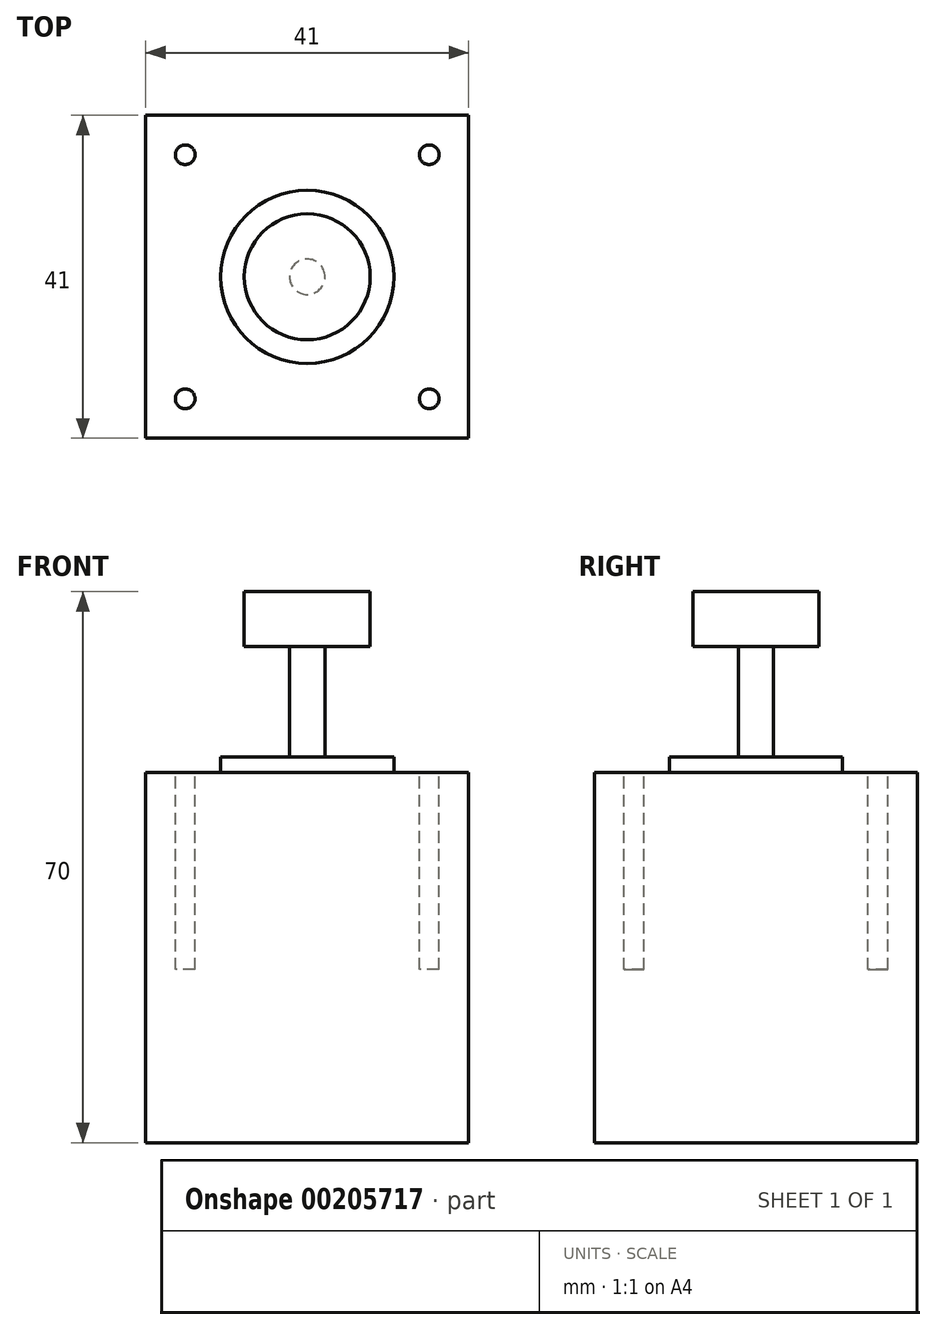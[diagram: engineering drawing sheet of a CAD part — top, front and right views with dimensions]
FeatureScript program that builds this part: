
annotation { "Feature Type Name" : "Feature", "Feature Type Description" : "" }
export const myFeature = defineFeature(function(context is Context, id is Id, definition is map)
    precondition{}
    {
        {
            var Q0;
            Q0=qCreatedBy(makeId("Top.planeOp"),FACE);
            var sketch = newSketch(context, id + "F0", { "sketchPlane" : qUnion([Q0])});
            skLineSegment(sketch, "E0.bottom", {"start": v(0, 0) * mm, "end": v(41, 0) * mm});
            skLineSegment(sketch, "E0.top", {"start": v(0, 41) * mm, "end": v(41, 41) * mm});
            skLineSegment(sketch, "E0.left", {"start": v(0, 0) * mm, "end": v(0, 41) * mm});
            skLineSegment(sketch, "E0.right", {"start": v(41, 0) * mm, "end": v(41, 41) * mm});
            skSolve(sketch);
        }
        {
            var Q0;
            Q0 = qSketchRegion(id + "F0", true);
            extrude(context, id + "F1", {"entities" : qUnion([Q0]), "depth" : 47 * mm});
        }
        {
            var Q0;
            Q0=makeQuery(id+"F1.opExtrude","CAP_FACE",FACE,{"disambiguationData":[OSD([sQuery(id+"F0.wireOp",EDGE,"E0.bottom"),sQuery(id+"F0.wireOp",EDGE,"E0.top"),sQuery(id+"F0.wireOp",EDGE,"E0.left"),sQuery(id+"F0.wireOp",EDGE,"E0.right")])],"isStart":false});
            var sketch = newSketch(context, id + "F2", { "sketchPlane" : qUnion([Q0])});
            skCircle(sketch, "E1", {"center": v(5, 5) * mm, "radius": 1.25 * mm});
            skLineSegment(sketch, "E2", {"start": v(0, 20.5) * mm, "end": v(20.5, 20.5) * mm, "construction": true});
            skPoint(sketch, "E2.endSnap0", {"position": v(20.5, 0) * mm});
            skLineSegment(sketch, "E3", {"start": v(20.5, 20.5) * mm, "end": v(20.5, 0) * mm, "construction": true});
            skCircle(sketch, "E4.1.0", {"center": v(36, 5) * mm, "radius": 1.25 * mm});
            skCircle(sketch, "E4.2.0", {"center": v(36, 36) * mm, "radius": 1.25 * mm});
            skCircle(sketch, "E4.3.0", {"center": v(5, 36) * mm, "radius": 1.25 * mm});
            skPoint(sketch, "E4.center", {"position": v(20.5, 20.5) * mm});
            skLineSegment(sketch, "E5", {"start": v(36, 36) * mm, "end": v(36, 5) * mm, "construction": true});
            skSolve(sketch);
        }
        {
            var Q0;
            Q0 = qSketchRegion(id + "F2", true);
            extrude(context, id + "F3", {"entities" : qUnion([Q0]), "operationType" : NewBodyOperationType.REMOVE, "oppositeDirection" : true, "depth" : 25 * mm});
        }
        {
            var Q0;
            Q0=makeQuery(id+"F1.opExtrude","CAP_FACE",FACE,{"disambiguationData":[OSD([sQuery(id+"F0.wireOp",EDGE,"E0.bottom"),sQuery(id+"F0.wireOp",EDGE,"E0.top"),sQuery(id+"F0.wireOp",EDGE,"E0.left"),sQuery(id+"F0.wireOp",EDGE,"E0.right")])],"isStart":false});
            var sketch = newSketch(context, id + "F4", { "sketchPlane" : qUnion([Q0])});
            skLineSegment(sketch, "E6", {"start": v(0, 20.5) * mm, "end": v(20.5, 20.5) * mm, "construction": true});
            skPoint(sketch, "E6.endSnap0", {"position": v(20.5, 0) * mm});
            skCircle(sketch, "E7", {"center": v(20.5, 20.5) * mm, "radius": 11 * mm});
            skSolve(sketch);
        }
        {
            var Q0;
            Q0 = qSketchRegion(id + "F4", true);
            extrude(context, id + "F5", {"entities" : qUnion([Q0]), "operationType" : NewBodyOperationType.ADD, "depth" : 2 * mm});
        }
        {
            var Q0;
            Q0=makeQuery(id+"F5.opExtrude","CAP_FACE",FACE,{"disambiguationData":[OSD([sQuery(id+"F4.wireOp",EDGE,"E7")])],"isStart":false});
            var sketch = newSketch(context, id + "F6", { "sketchPlane" : qUnion([Q0])});
            skCircle(sketch, "E8", {"center": v(20.5, 20.5) * mm, "radius": 2.25 * mm});
            skSolve(sketch);
        }
        {
            var Q0;
            Q0 = qSketchRegion(id + "F6", true);
            extrude(context, id + "F7", {"entities" : qUnion([Q0]), "operationType" : NewBodyOperationType.ADD, "depth" : 21 * mm});
        }
        {
            var Q0;
            Q0=makeQuery(id+"F7.opExtrude","CAP_FACE",FACE,{"disambiguationData":[OSD([sQuery(id+"F6.wireOp",EDGE,"E8")])],"isStart":false});
            var sketch = newSketch(context, id + "F8", { "sketchPlane" : qUnion([Q0])});
            skCircle(sketch, "E9", {"center": v(20.5, 20.5) * mm, "radius": 8 * mm});
            skCircle(sketch, "E10", {"center": v(20.5, 20.5) * mm, "radius": 5.75 * mm, "construction": true});
            skSolve(sketch);
        }
        {
            var Q0;
            Q0 = qSketchRegion(id + "F8", true);
            extrude(context, id + "F9", {"entities" : qUnion([Q0]), "operationType" : NewBodyOperationType.ADD, "oppositeDirection" : true, "depth" : 7 * mm});
        }
    });
